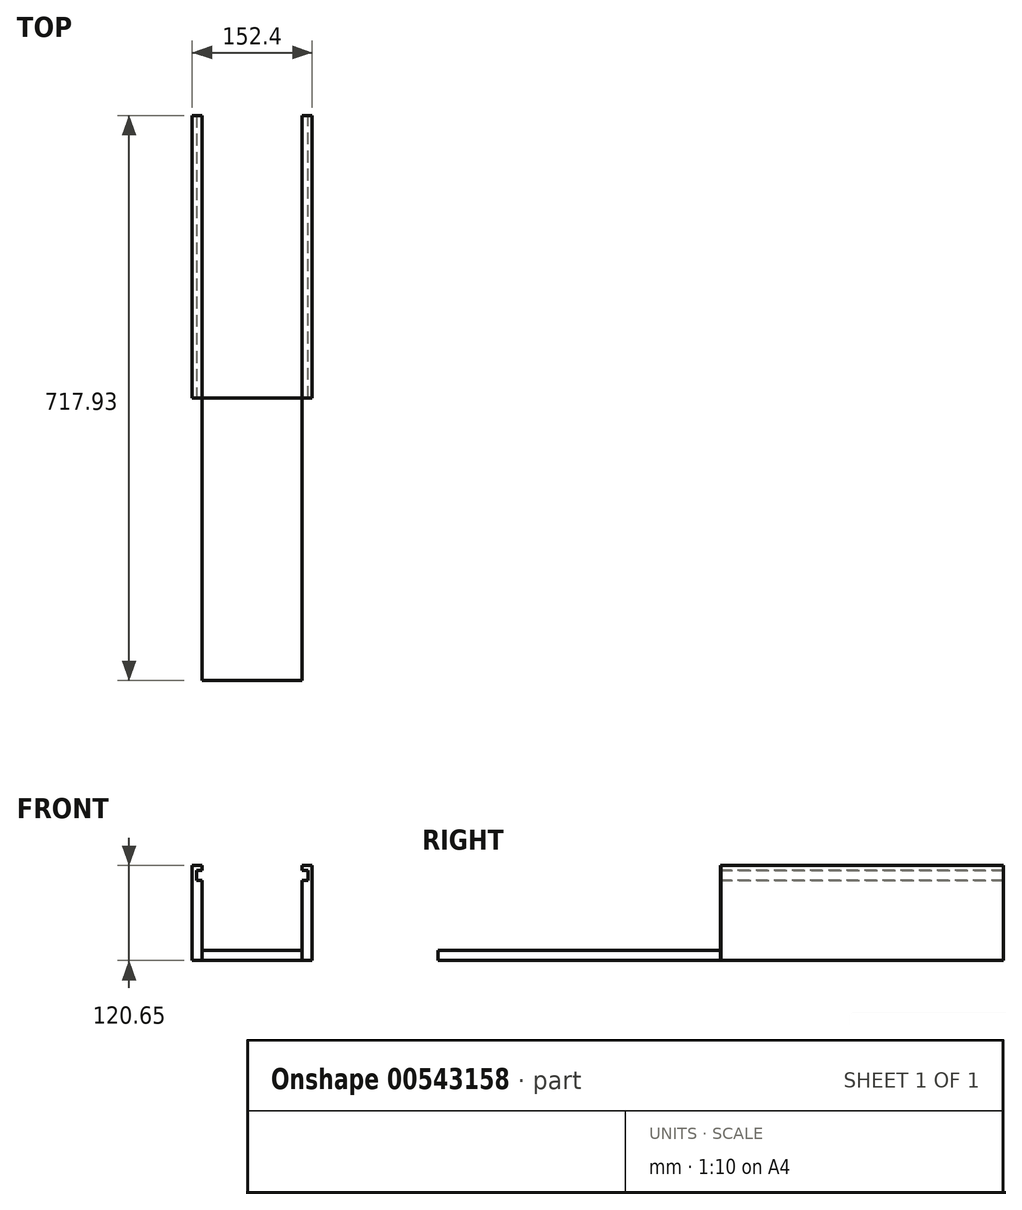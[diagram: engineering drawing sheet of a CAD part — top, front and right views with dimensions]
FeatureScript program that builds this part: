
annotation { "Feature Type Name" : "Feature", "Feature Type Description" : "" }
export const myFeature = defineFeature(function(context is Context, id is Id, definition is map)
    precondition{}
    {
        {
            var Q0;
            Q0=qCreatedBy(makeId("Front.planeOp"),FACE);
            var sketch = newSketch(context, id + "F0", { "sketchPlane" : qUnion([Q0])});
            skLineSegment(sketch, "E0", {"start": v(59.72, 61.48) * mm, "end": v(59.72, -59.17) * mm});
            skLineSegment(sketch, "E1", {"start": v(59.72, -59.17) * mm, "end": v(47.02, -59.17) * mm});
            skLineSegment(sketch, "E2", {"start": v(47.02, -59.17) * mm, "end": v(47.02, 42.43) * mm});
            skLineSegment(sketch, "E3", {"start": v(47.02, 42.43) * mm, "end": v(54.31, 42.43) * mm});
            skLineSegment(sketch, "E4", {"start": v(54.31, 42.43) * mm, "end": v(54.31, 55.13) * mm});
            skLineSegment(sketch, "E5", {"start": v(54.31, 55.13) * mm, "end": v(47.02, 55.13) * mm});
            skLineSegment(sketch, "E6", {"start": v(47.02, 55.13) * mm, "end": v(47.02, 61.48) * mm});
            skLineSegment(sketch, "E7", {"start": v(47.02, 61.48) * mm, "end": v(59.72, 61.48) * mm});
            skSolve(sketch);
        }
        {
            var Q0;
            Q0=makeQuery(id+"F0.imprint","IMPRINT",FACE,{"disambiguationData":[TD([[makeQuery(id+"F0.imprint","IMPRINT",EDGE,{"derivedFrom":sQuery(id+"F0.wireOp",EDGE,"E0")}),-1.0]])]});
            extrude(context, id + "F1", {"entities" : qUnion([Q0]), "depth" : 358.77 * mm, "offsetDistance" : 25.4 * mm});
        }
        {
            var Q0;
            Q0=makeQuery(id+"F1.opExtrude","SWEPT_BODY",BODY,{"disambiguationData":[OSD([sQuery(id+"F0.wireOp",EDGE,"E0"),sQuery(id+"F0.wireOp",EDGE,"E1"),sQuery(id+"F0.wireOp",EDGE,"E2"),sQuery(id+"F0.wireOp",EDGE,"E3"),sQuery(id+"F0.wireOp",EDGE,"E4"),sQuery(id+"F0.wireOp",EDGE,"E5"),sQuery(id+"F0.wireOp",EDGE,"E6"),sQuery(id+"F0.wireOp",EDGE,"E7")])]});
            var Q1;
            Q1=makeQuery(id+"F1.opExtrude","CAP_EDGE",EDGE,{"disambiguationData":[OSD([sQuery(id+"F0.wireOp",EDGE,"E2")])],"isStart":true});
            var Q2;
            Q2=qCreatedBy(makeId("Right.planeOp"),FACE);
            transform(context, id + "F2", {"entities" : qUnion([Q0]), "transformType" : TransformType.ROTATION, "transformAxis" : qUnion([Q1]), "angle" : 180 * degree, "oppositeDirection" : true, "makeCopy" : true});
        }
        {
            var Q0;
            Q0=makeQuery(id+"F2.opPattern","COPY",BODY,{"derivedFrom":makeQuery(id+"F1.opExtrude","SWEPT_BODY",BODY,{"disambiguationData":[OSD([sQuery(id+"F0.wireOp",EDGE,"E0"),sQuery(id+"F0.wireOp",EDGE,"E1"),sQuery(id+"F0.wireOp",EDGE,"E2"),sQuery(id+"F0.wireOp",EDGE,"E3"),sQuery(id+"F0.wireOp",EDGE,"E4"),sQuery(id+"F0.wireOp",EDGE,"E5"),sQuery(id+"F0.wireOp",EDGE,"E6"),sQuery(id+"F0.wireOp",EDGE,"E7")])]}),"instanceName":"1"});
            var Q1;
            Q1=qCreatedBy(makeId("Right.planeOp"),FACE);
            transform(context, id + "F3", {"entities" : qUnion([Q0]), "transformType" : TransformType.TRANSLATION_DISTANCE, "transformDirection" : qUnion([Q1]), "distance" : 127 * mm, "oppositeDirection" : true, "makeCopy" : false});
        }
        {
            var Q0;
            Q0=qCreatedBy(makeId("Front.planeOp"),FACE);
            var sketch = newSketch(context, id + "F4", { "sketchPlane" : qUnion([Q0])});
            skLineSegment(sketch, "E8.bottom", {"start": v(46.94, -46.45) * mm, "end": v(-80.06, -46.45) * mm});
            skLineSegment(sketch, "E8.top", {"start": v(46.94, -59.15) * mm, "end": v(-80.06, -59.15) * mm});
            skLineSegment(sketch, "E8.left", {"start": v(46.94, -46.45) * mm, "end": v(46.94, -59.15) * mm});
            skLineSegment(sketch, "E8.right", {"start": v(-80.06, -46.45) * mm, "end": v(-80.06, -59.15) * mm});
            skSolve(sketch);
        }
        {
            var Q0;
            Q0=makeQuery(id+"F4.imprint","IMPRINT",FACE,{"disambiguationData":[TD([[makeQuery(id+"F4.imprint","IMPRINT",EDGE,{"derivedFrom":sQuery(id+"F4.wireOp",EDGE,"E8.bottom")}),1.0]])]});
            extrude(context, id + "F5", {"entities" : qUnion([Q0]), "operationType" : NewBodyOperationType.ADD, "depth" : 358.77 * mm, "offsetDistance" : 25.4 * mm});
        }
        {
            var Q0;
            Q0=makeQuery(id+"F2.opPattern","COPY",EDGE,{"derivedFrom":makeQuery(id+"F1.opExtrude","CAP_EDGE",EDGE,{"disambiguationData":[OSD([sQuery(id+"F0.wireOp",EDGE,"E0")])],"isStart":true}),"instanceName":"1"});
            cPoint(context, id + "F6", {"entities" : qUnion([Q0]), "parameter" : 0.5});
        }
        {
            var Q0;
            Q0=makeQuery(id+"F2.opPattern","COPY",BODY,{"derivedFrom":makeQuery(id+"F1.opExtrude","SWEPT_BODY",BODY,{"disambiguationData":[OSD([sQuery(id+"F0.wireOp",EDGE,"E0"),sQuery(id+"F0.wireOp",EDGE,"E1"),sQuery(id+"F0.wireOp",EDGE,"E2"),sQuery(id+"F0.wireOp",EDGE,"E3"),sQuery(id+"F0.wireOp",EDGE,"E4"),sQuery(id+"F0.wireOp",EDGE,"E5"),sQuery(id+"F0.wireOp",EDGE,"E6"),sQuery(id+"F0.wireOp",EDGE,"E7")])]}),"instanceName":"1"});
            var Q1;
            Q1 = qCreatedBy(id + "F6" ,VERTEX);
            var Q2;
            Q2=makeQuery(id+"F1.opExtrude","CAP_EDGE",EDGE,{"disambiguationData":[OSD([sQuery(id+"F0.wireOp",EDGE,"E2")])],"isStart":false});
            transform(context, id + "F7", {"entities" : qUnion([Q0]), "transformType" : TransformType.TRANSLATION_3D, "dx" : 0 * mm, "dy" : -359.16 * mm, "dz" : 0 * mm, "makeCopy" : false});
        }
    });
